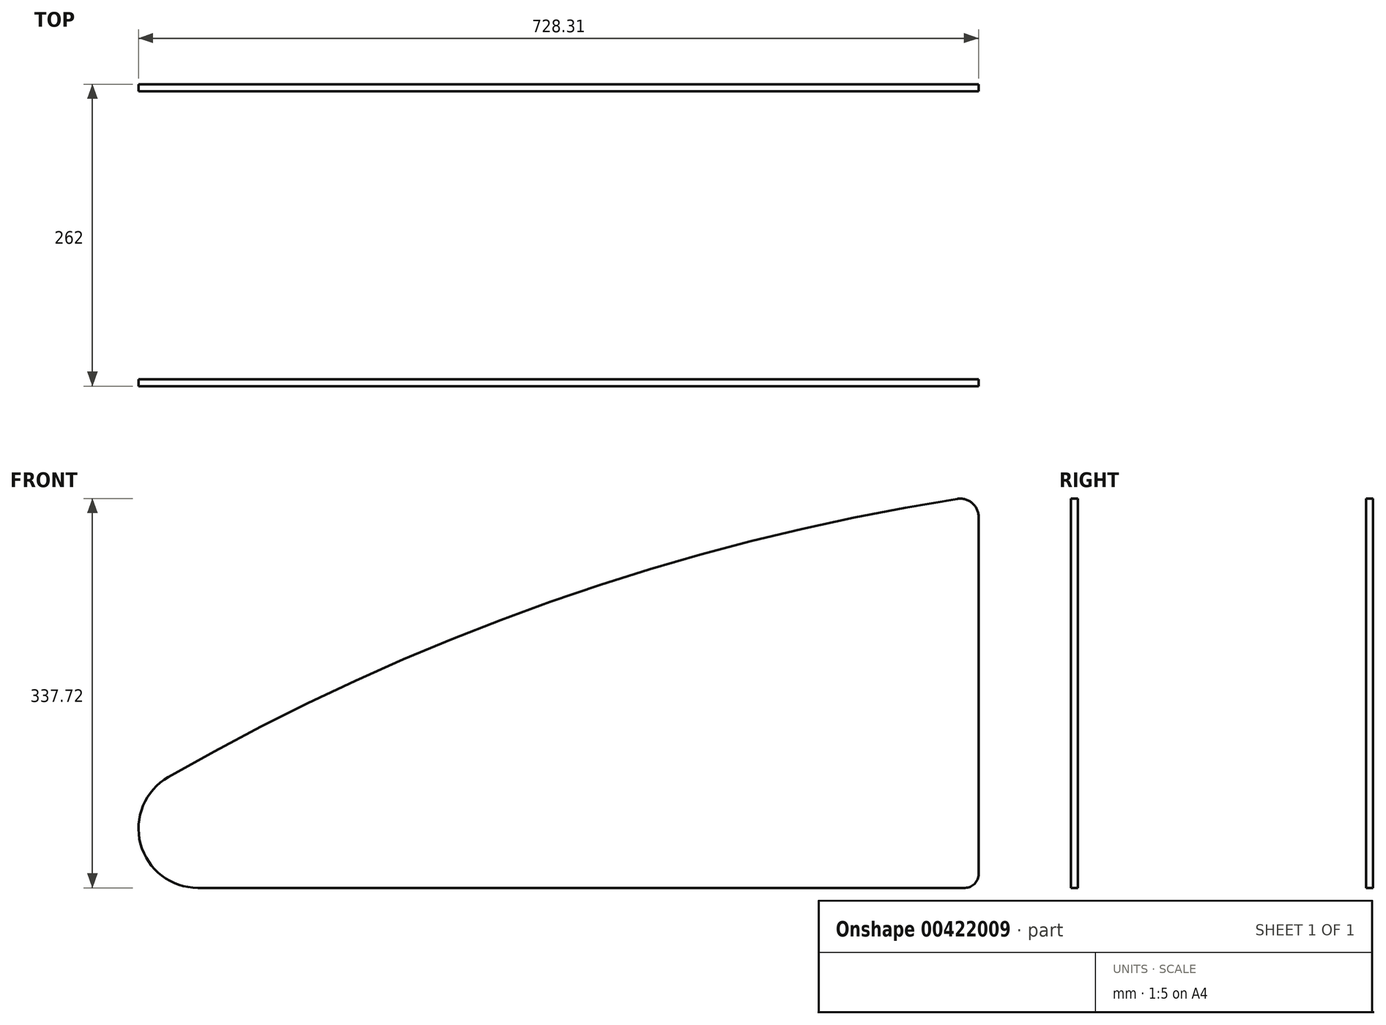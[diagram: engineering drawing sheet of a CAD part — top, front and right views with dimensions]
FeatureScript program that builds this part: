
annotation { "Feature Type Name" : "Feature", "Feature Type Description" : "" }
export const myFeature = defineFeature(function(context is Context, id is Id, definition is map)
    precondition{}
    {
        {
            var Q0;
            Q0=qCreatedBy(makeId("Front.planeOp"),FACE);
            cPlane(context, id + "F0", {"entities" : qUnion([Q0]), "cplaneType" : CPlaneType.OFFSET, "offset" : 247 * mm, "oppositeDirection" : true, "width" : 152.4 * mm, "height" : 152.4 * mm});
        }
        {
            var Q0;
            Q0=qCreatedBy(id+"F0.planeOp",FACE);
            var sketch = newSketch(context, id + "F1", { "sketchPlane" : qUnion([Q0])});
            skPoint(sketch, "E0", {"position": v(-811.76, 74.53) * mm});
            skPoint(sketch, "E1", {"position": v(-800, 86.3) * mm});
            skPoint(sketch, "E2", {"position": v(-800, 396.3) * mm});
            skPoint(sketch, "E3", {"position": v(-1476.86, 74.53) * mm});
            skPoint(sketch, "E4", {"position": v(-818.46, 412.05) * mm});
            skPoint(sketch, "E5", {"position": v(-1502.48, 170.6) * mm});
            skLineSegment(sketch, "E6", {"start": v(-811.76, 74.53) * mm, "end": v(-1476.86, 74.53) * mm});
            skLineSegment(sketch, "E7", {"start": v(-800, 86.3) * mm, "end": v(-800, 396.3) * mm});
            skArc(sketch, "E8", {"start": v(-811.76, 74.53) * mm, "mid": v(-803.44, 77.98) * mm, "end": v(-800, 86.3) * mm});
            skArc(sketch, "E9", {"start": v(-800, 396.3) * mm, "mid": v(-805.6, 408.43) * mm, "end": v(-818.46, 412.05) * mm});
            skArc(sketch, "E10", {"start": v(-818.46, 412.05) * mm, "mid": v(-1171.49, 322.54) * mm, "end": v(-1502.48, 170.6) * mm});
            skArc(sketch, "E11", {"start": v(-1502.48, 170.6) * mm, "mid": v(-1526.57, 112.72) * mm, "end": v(-1476.86, 74.53) * mm});
            skSolve(sketch);
        }
        {
            var Q0;
            Q0=makeQuery(id+"F1.imprint","IMPRINT",FACE,{"disambiguationData":[TD([[makeQuery(id+"F1.imprint","IMPRINT",EDGE,{"derivedFrom":sQuery(id+"F1.wireOp",EDGE,"E6")}),-1.0]])]});
            extrude(context, id + "F2", {"entities" : qUnion([Q0]), "oppositeDirection" : true, "depth" : 6 * mm});
        }
        {
            var Q0;
            Q0=qCreatedBy(makeId("Front.planeOp"),FACE);
            cPlane(context, id + "F3", {"entities" : qUnion([Q0]), "cplaneType" : CPlaneType.OFFSET, "offset" : 378 * mm, "oppositeDirection" : true, "width" : 150 * mm, "height" : 150 * mm});
        }
        {
            var Q0;
            Q0=makeQuery(id+"F2.opExtrude","SWEPT_BODY",BODY,{"disambiguationData":[OSD([sQuery(id+"F1.wireOp",EDGE,"E6"),sQuery(id+"F1.wireOp",EDGE,"E7"),sQuery(id+"F1.wireOp",EDGE,"E8"),sQuery(id+"F1.wireOp",EDGE,"E9"),sQuery(id+"F1.wireOp",EDGE,"E10"),sQuery(id+"F1.wireOp",EDGE,"E11")])]});
            var Q1;
            Q1=qCreatedBy(id+"F3.planeOp",FACE);
            mirror(context, id + "F4", {"entities" : qUnion([Q0]), "mirrorPlane" : qUnion([Q1])});
        }
    });
